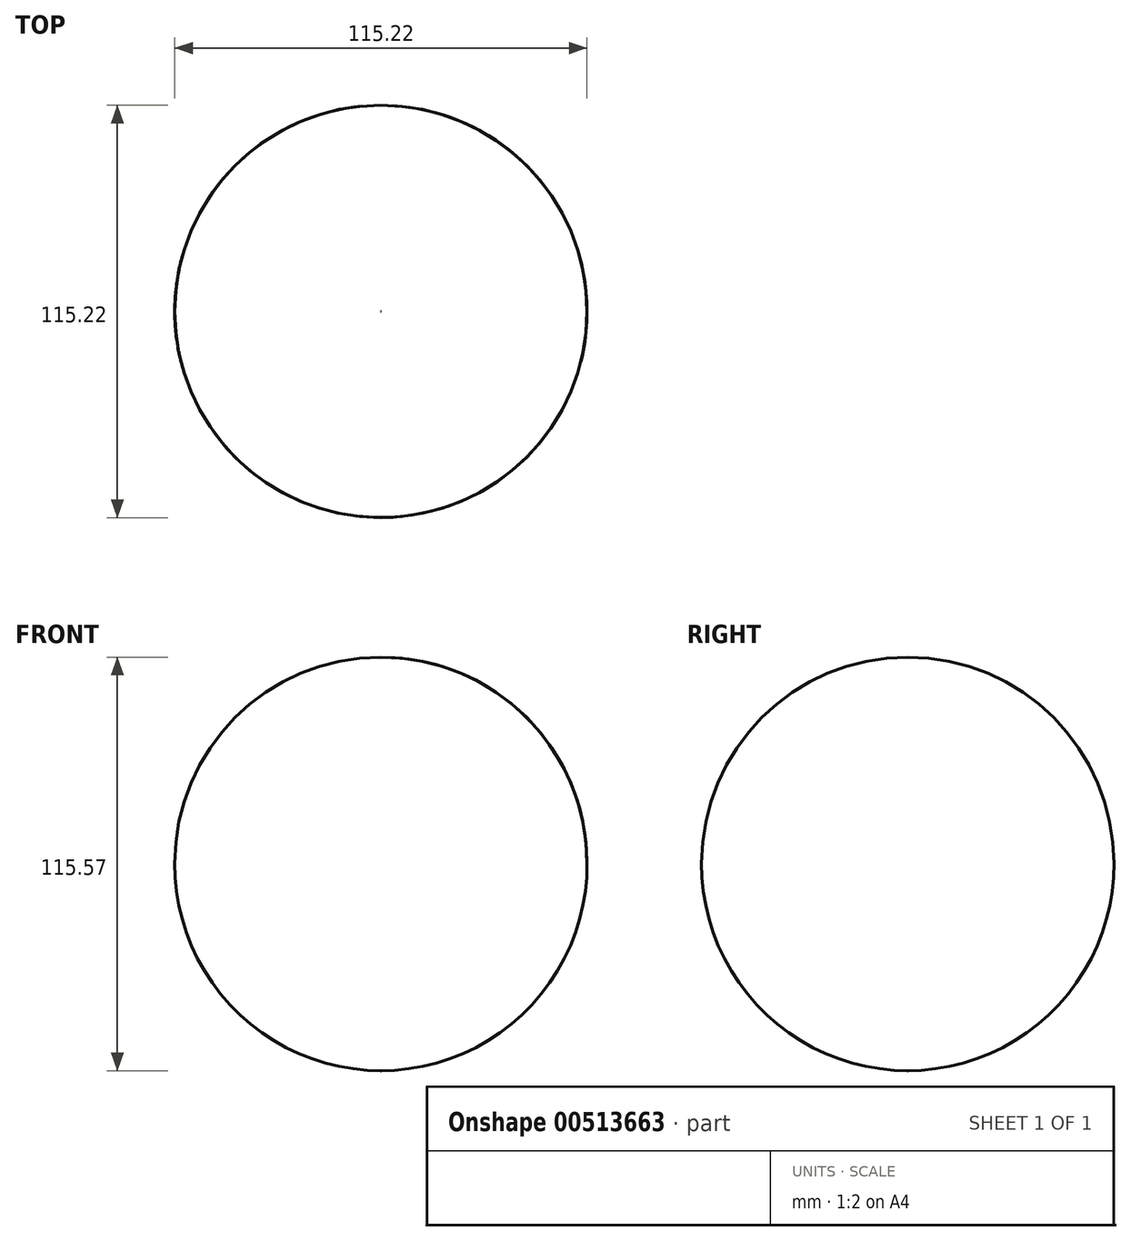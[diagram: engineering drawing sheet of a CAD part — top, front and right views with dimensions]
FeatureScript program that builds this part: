
annotation { "Feature Type Name" : "Feature", "Feature Type Description" : "" }
export const myFeature = defineFeature(function(context is Context, id is Id, definition is map)
    precondition{}
    {
        {
            var Q0;
            Q0=qCreatedBy(makeId("Front.planeOp"),FACE);
            var sketch = newSketch(context, id + "F0", { "sketchPlane" : qUnion([Q0])});
            skArc(sketch, "E0", {"start": v(57.6, 0) * mm, "mid": v(40.73, 40.73) * mm, "end": v(0, 57.6) * mm});
            skArc(sketch, "E1", {"start": v(0, -57.96) * mm, "mid": v(40.85, -40.95) * mm, "end": v(57.6, 0) * mm});
            skLineSegment(sketch, "E2", {"start": v(0, 57.6) * mm, "end": v(0, -57.96) * mm, "construction": true});
            skLineSegment(sketch, "E3", {"start": v(0, 57.6) * mm, "end": v(0, -57.96) * mm});
            skSolve(sketch);
        }
        {
            var Q0;
            Q0 = qSketchRegion(id + "F0", true);
            var Q1;
            Q1=sQuery(id+"F0.wireOp",EDGE,"E2");
            revolve(context, id + "F1", {"entities" : qUnion([Q0]), "axis" : qUnion([Q1]), "revolveType" : RevolveType.FULL});
        }
    });
